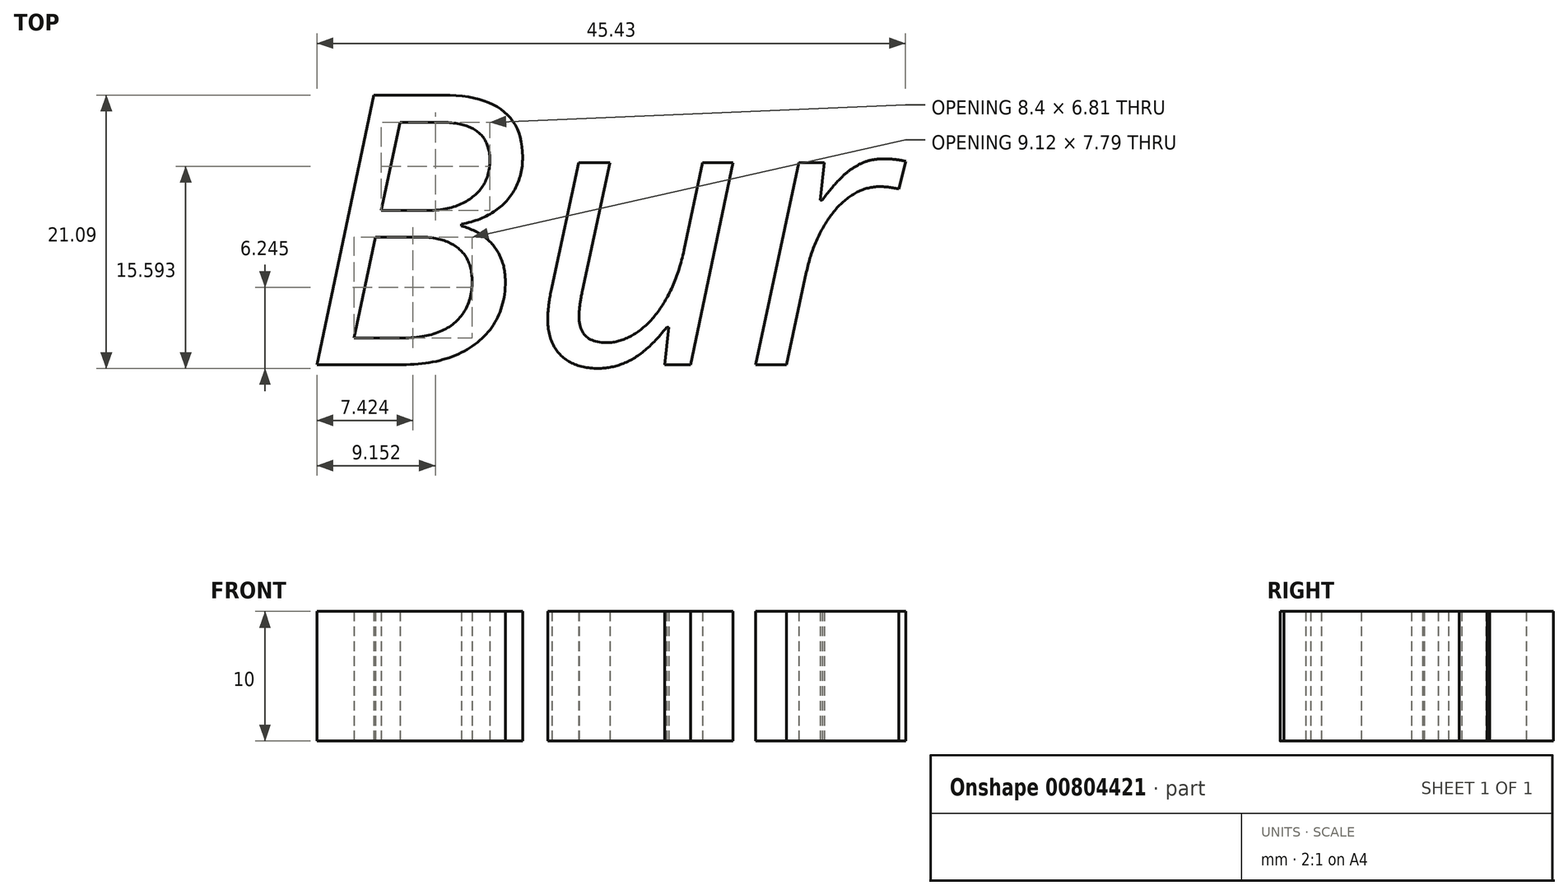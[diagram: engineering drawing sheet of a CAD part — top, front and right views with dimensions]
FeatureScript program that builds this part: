
annotation { "Feature Type Name" : "Feature", "Feature Type Description" : "" }
export const myFeature = defineFeature(function(context is Context, id is Id, definition is map)
    precondition{}
    {
        {
            var Q0;
            Q0=qCreatedBy(makeId("Top.planeOp"),FACE);
            var sketch = newSketch(context, id + "F0", { "sketchPlane" : qUnion([Q0])});
            skText(sketch, "E0", { "text": "Bur", "fontName": "OpenSans-Italic.ttf"});
            const initialGuessF0  = {"E0": [-0.05992, 0.01538, 1, 0, 0.02098]};
            skSetInitialGuess(sketch, initialGuessF0);
            skSolve(sketch);
        }
        {
            var Q0;
            Q0 = qSketchRegion(id + "F0", true);
            extrude(context, id + "F1", {"entities" : qUnion([Q0]), "depth" : 10 * mm, "offsetDistance" : 25 * mm});
        }
    });
